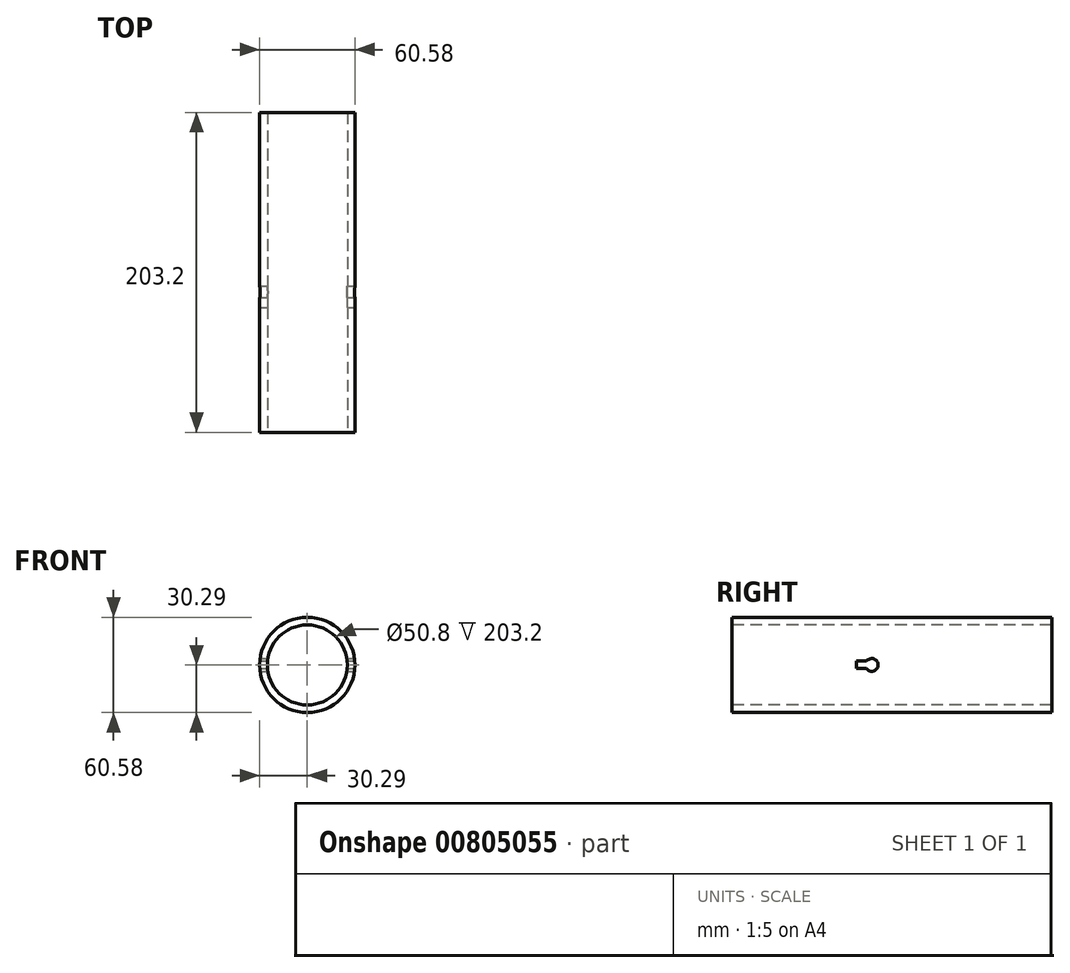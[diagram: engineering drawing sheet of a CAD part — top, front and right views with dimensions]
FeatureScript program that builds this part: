
annotation { "Feature Type Name" : "Feature", "Feature Type Description" : "" }
export const myFeature = defineFeature(function(context is Context, id is Id, definition is map)
    precondition{}
    {
        {
            var Q0;
            Q0=qCreatedBy(makeId("Front.planeOp"),FACE);
            var sketch = newSketch(context, id + "F0", { "sketchPlane" : qUnion([Q0])});
            skCircle(sketch, "E0", {"center": v(0, 0) * mm, "radius": 30.29 * mm});
            skSolve(sketch);
        }
        {
            var Q0;
            Q0=makeQuery(id+"F0.imprint","IMPRINT",FACE,{"disambiguationData":[TD([[makeQuery(id+"F0.imprint","IMPRINT",EDGE,{"derivedFrom":sQuery(id+"F0.wireOp",EDGE,"E0")}),1.0]])]});
            extrude(context, id + "F1", {"entities" : qUnion([Q0]), "depth" : 203.2 * mm, "offsetDistance" : 25.4 * mm});
        }
        {
            var Q0;
            Q0=makeQuery(id+"F1.opExtrude","CAP_FACE",FACE,{"disambiguationData":[OSD([sQuery(id+"F0.wireOp",EDGE,"E0")])],"isStart":false});
            var sketch = newSketch(context, id + "F2", { "sketchPlane" : qUnion([Q0])});
            skCircle(sketch, "E1", {"center": v(0, 0) * mm, "radius": 25.4 * mm});
            skSolve(sketch);
        }
        {
            var Q0;
            Q0=makeQuery(id+"F2.imprint","IMPRINT",FACE,{"disambiguationData":[TD([[makeQuery(id+"F2.imprint","IMPRINT",EDGE,{"derivedFrom":sQuery(id+"F2.wireOp",EDGE,"E1")}),1.0]])]});
            extrude(context, id + "F3", {"entities" : qUnion([Q0]), "operationType" : NewBodyOperationType.REMOVE, "endBound" : BoundingType.THROUGH_ALL, "oppositeDirection" : true, "depth" : 25.4 * mm, "offsetDistance" : 25.4 * mm});
        }
        {
            var Q0;
            Q0=qCreatedBy(makeId("Right.planeOp"),FACE);
            var sketch = newSketch(context, id + "F4", { "sketchPlane" : qUnion([Q0])});
            skCircle(sketch, "E2", {"center": v(-114.3, 0) * mm, "radius": 4.06 * mm});
            skLineSegment(sketch, "E3.bottom", {"start": v(-117.57, 2.4) * mm, "end": v(-123.92, 2.4) * mm});
            skLineSegment(sketch, "E3.top", {"start": v(-117.57, -2.16) * mm, "end": v(-123.92, -2.16) * mm});
            skLineSegment(sketch, "E3.left", {"start": v(-117.57, 2.4) * mm, "end": v(-117.57, -2.16) * mm});
            skLineSegment(sketch, "E3.right", {"start": v(-123.92, 2.4) * mm, "end": v(-123.92, -2.16) * mm});
            skSolve(sketch);
        }
        {
            var Q0;
            Q0 = qSketchRegion(id + "F4", true);
            extrude(context, id + "F5", {"entities" : qUnion([Q0]), "operationType" : NewBodyOperationType.REMOVE, "endBound" : BoundingType.THROUGH_ALL, "oppositeDirection" : true, "depth" : 25.4 * mm, "offsetDistance" : 25.4 * mm, "hasSecondDirection" : true, "secondDirectionBound" : SecondDirectionBoundingType.THROUGH_ALL, "secondDirectionOppositeDirection" : false, "secondDirectionDepth" : 25.4 * mm});
        }
    });
